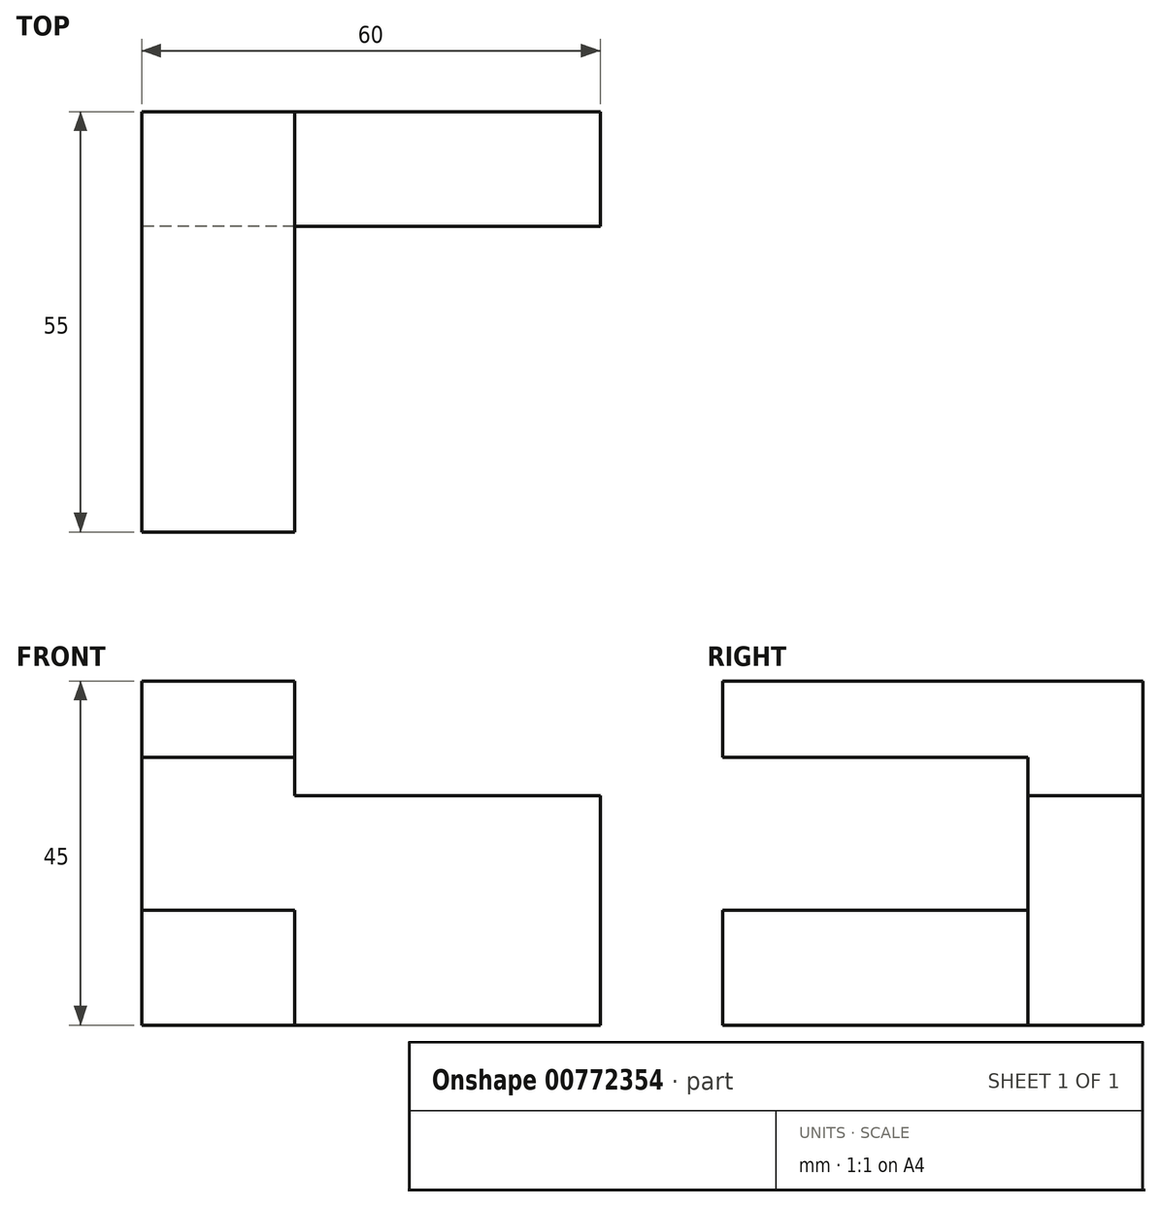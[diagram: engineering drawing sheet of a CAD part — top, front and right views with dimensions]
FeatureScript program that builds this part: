
annotation { "Feature Type Name" : "Feature", "Feature Type Description" : "" }
export const myFeature = defineFeature(function(context is Context, id is Id, definition is map)
    precondition{}
    {
        {
            var Q0;
            Q0=qCreatedBy(makeId("Right.planeOp"),FACE);
            var sketch = newSketch(context, id + "F0", { "sketchPlane" : qUnion([Q0])});
            skLineSegment(sketch, "E0", {"start": v(0, 0) * mm, "end": v(0, 45) * mm});
            skLineSegment(sketch, "E1", {"start": v(0, 45) * mm, "end": v(-55, 45) * mm});
            skLineSegment(sketch, "E2", {"start": v(-55, 45) * mm, "end": v(-55, 35) * mm});
            skLineSegment(sketch, "E3", {"start": v(-55, 35) * mm, "end": v(-15, 35) * mm});
            skLineSegment(sketch, "E4", {"start": v(-15, 35) * mm, "end": v(-15, 15) * mm});
            skLineSegment(sketch, "E5", {"start": v(-15, 15) * mm, "end": v(-55, 15) * mm});
            skLineSegment(sketch, "E6", {"start": v(-55, 15) * mm, "end": v(-55, 0) * mm});
            skLineSegment(sketch, "E7", {"start": v(-55, 0) * mm, "end": v(0, 0) * mm});
            skLineSegment(sketch, "E8", {"start": v(-15, 30) * mm, "end": v(0, 30) * mm});
            skLineSegment(sketch, "E9", {"start": v(-15, 15) * mm, "end": v(-15, 0) * mm});
            skSolve(sketch);
        }
        {
            var Q0;
            {var subQ1=sQuery(id+"F0.wireOp",EDGE,"E1");Q0=makeQuery(id+"F0.imprint","IMPRINT",FACE,{"disambiguationData":[TD([[makeQuery(id+"F0.imprint","IMPRINT",EDGE,{"derivedFrom":subQ1}),1.0]])]});}
            var Q1;
            Q1=makeQuery(id+"F0.imprint","IMPRINT",FACE,{"disambiguationData":[TD([[makeQuery(id+"F0.imprint","IMPRINT",EDGE,{"derivedFrom":sQuery(id+"F0.wireOp",EDGE,"E5")}),1.0]])]});
            extrude(context, id + "F1", {"entities" : qUnion([Q0, Q1]), "depth" : 20 * mm, "offsetDistance" : 25 * mm});
        }
        {
            var Q0;
            {var subQ0=sQuery(id+"F0.wireOp",EDGE,"E8");Q0=makeQuery(id+"F0.imprint","IMPRINT",FACE,{"disambiguationData":[TD([[makeQuery(id+"F0.imprint","IMPRINT",EDGE,{"derivedFrom":subQ0}),-1.0]])]});}
            extrude(context, id + "F2", {"entities" : qUnion([Q0]), "operationType" : NewBodyOperationType.ADD, "depth" : 60 * mm, "offsetDistance" : 25 * mm});
        }
    });
